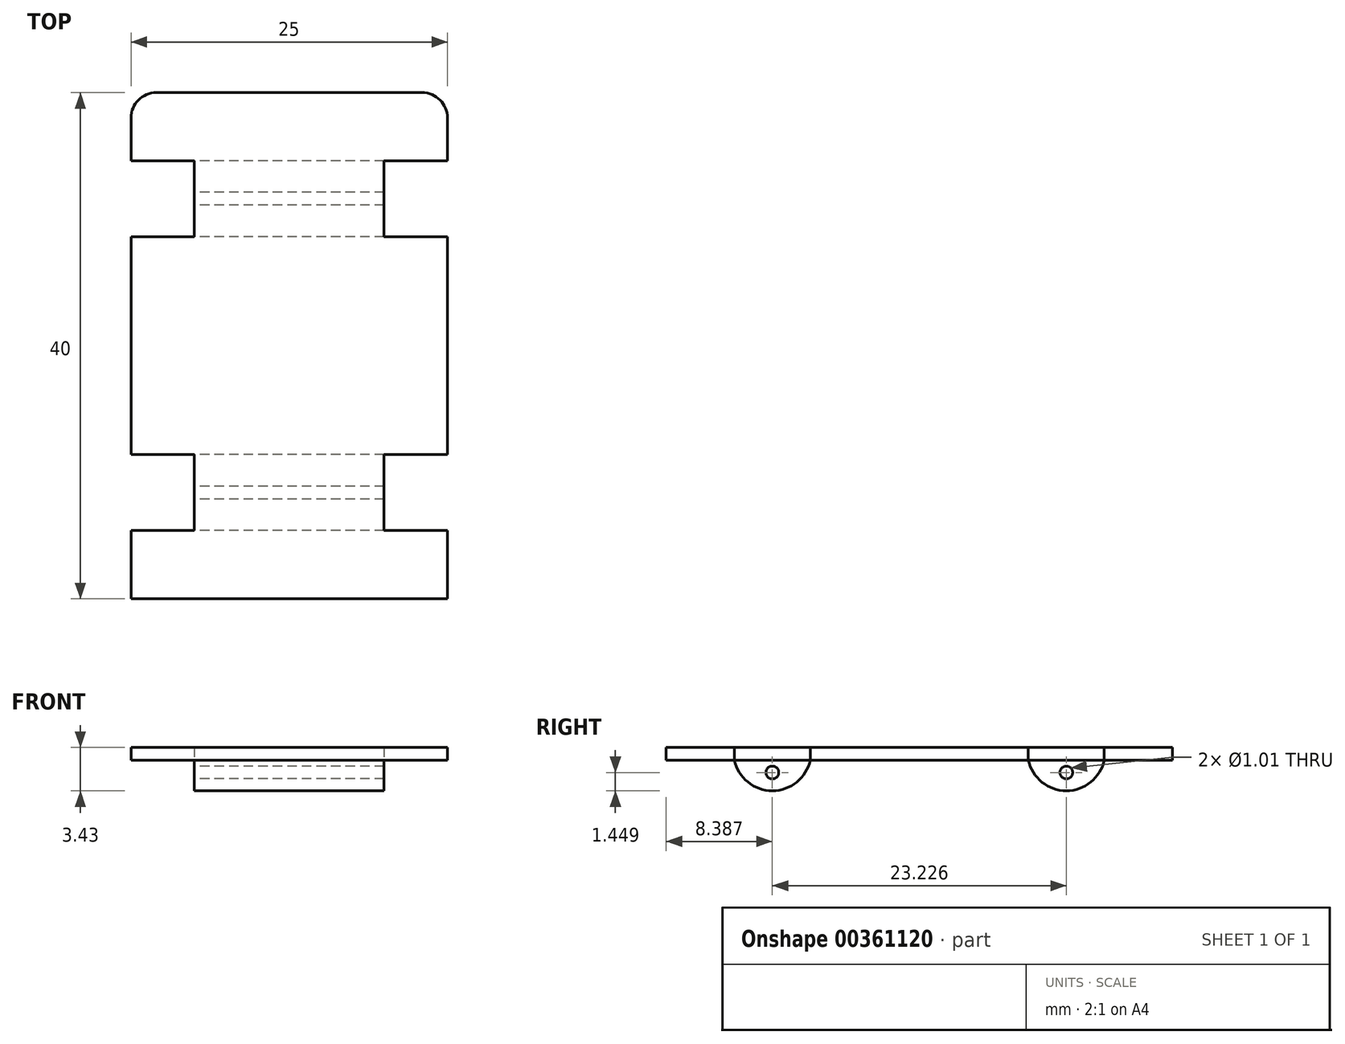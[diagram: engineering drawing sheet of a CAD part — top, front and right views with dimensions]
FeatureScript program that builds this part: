
annotation { "Feature Type Name" : "Feature", "Feature Type Description" : "" }
export const myFeature = defineFeature(function(context is Context, id is Id, definition is map)
    precondition{}
    {
        {
            var Q0;
            Q0=qCreatedBy(makeId("Top.planeOp"),FACE);
            var sketch = newSketch(context, id + "F0", { "sketchPlane" : qUnion([Q0])});
            skLineSegment(sketch, "E0.bottom", {"start": v(10.5, 20) * mm, "end": v(-10.5, 20) * mm});
            skLineSegment(sketch, "E0.top", {"start": v(12.5, -20) * mm, "end": v(-12.5, -20) * mm});
            skLineSegment(sketch, "E0.left", {"start": v(12.5, 18) * mm, "end": v(12.5, 14.61) * mm});
            skLineSegment(sketch, "E0.right", {"start": v(-12.5, 18) * mm, "end": v(-12.5, 14.61) * mm});
            skPoint(sketch, "E0.middle", {"position": v(0, 0) * mm});
            skLineSegment(sketch, "E1.bottom", {"start": v(-12.5, 14.61) * mm, "end": v(-7.5, 14.61) * mm});
            skLineSegment(sketch, "E1.top", {"start": v(-12.5, 8.61) * mm, "end": v(-7.5, 8.61) * mm});
            skLineSegment(sketch, "E1.right", {"start": v(-7.5, 14.61) * mm, "end": v(-7.5, 8.61) * mm});
            skLineSegment(sketch, "E2.MirrorCS", {"start": v(12.5, 14.61) * mm, "end": v(7.5, 14.61) * mm});
            skLineSegment(sketch, "E3.MirrorCS", {"start": v(7.5, 14.61) * mm, "end": v(7.5, 8.61) * mm});
            skLineSegment(sketch, "E4.MirrorCS", {"start": v(12.5, 8.61) * mm, "end": v(7.5, 8.61) * mm});
            skLineSegment(sketch, "E5.MirrorCS", {"start": v(-12.5, -14.61) * mm, "end": v(-7.5, -14.61) * mm});
            skLineSegment(sketch, "E6.MirrorCS", {"start": v(-7.5, -14.61) * mm, "end": v(-7.5, -8.61) * mm});
            skLineSegment(sketch, "E7.MirrorCS", {"start": v(-12.5, -8.61) * mm, "end": v(-7.5, -8.61) * mm});
            skLineSegment(sketch, "E8.MirrorCS", {"start": v(12.5, -14.61) * mm, "end": v(7.5, -14.61) * mm});
            skLineSegment(sketch, "E9.MirrorCS", {"start": v(7.5, -14.61) * mm, "end": v(7.5, -8.61) * mm});
            skLineSegment(sketch, "E10.MirrorCS", {"start": v(12.5, -8.61) * mm, "end": v(7.5, -8.61) * mm});
            skLineSegment(sketch, "E11.trimOffspring", {"start": v(-12.5, 8.61) * mm, "end": v(-12.5, -8.61) * mm});
            skLineSegment(sketch, "E12.trimOffspring", {"start": v(12.5, 8.61) * mm, "end": v(12.5, -8.61) * mm});
            skLineSegment(sketch, "E13.trimOffspring", {"start": v(12.5, -14.61) * mm, "end": v(12.5, -20) * mm});
            skLineSegment(sketch, "E14.trimOffspring", {"start": v(-12.5, -14.61) * mm, "end": v(-12.5, -20) * mm});
            skPoint(sketch, "E15.visualSharp", {"position": v(-12.5, 20) * mm});
            skArc(sketch, "E15.filletArc", {"start": v(-10.5, 20) * mm, "mid": v(-11.91, 19.41) * mm, "end": v(-12.5, 18) * mm});
            skPoint(sketch, "E16.visualSharp", {"position": v(12.5, 20) * mm});
            skArc(sketch, "E16.filletArc", {"start": v(12.5, 18) * mm, "mid": v(11.91, 19.41) * mm, "end": v(10.5, 20) * mm});
            skSolve(sketch);
        }
        {
            var Q0;
            Q0 = qSketchRegion(id + "F0", true);
            extrude(context, id + "F1", {"entities" : qUnion([Q0]), "endBound" : BoundingType.SYMMETRIC, "depth" : 1 * mm});
        }
        {
            var Q0;
            Q0=qCreatedBy(makeId("Right.planeOp"),FACE);
            var sketch = newSketch(context, id + "F2", { "sketchPlane" : qUnion([Q0])});
            skArc(sketch, "E17", {"start": v(-14.62, -0.5) * mm, "mid": v(-11.62, -2.93) * mm, "end": v(-8.61, -0.5) * mm});
            skLineSegment(sketch, "E18", {"start": v(-14.62, -0.5) * mm, "end": v(-8.61, -0.5) * mm});
            skCircle(sketch, "E19", {"center": v(-11.61, -1.48) * mm, "radius": 0.5 * mm});
            skArc(sketch, "E20.MirrorCS", {"start": v(14.62, -0.5) * mm, "mid": v(11.62, -2.93) * mm, "end": v(8.61, -0.5) * mm});
            skCircle(sketch, "E21.MirrorC", {"center": v(11.61, -1.48) * mm, "radius": 0.5 * mm});
            skLineSegment(sketch, "E22.MirrorCS", {"start": v(14.62, -0.5) * mm, "end": v(8.61, -0.5) * mm});
            skSolve(sketch);
        }
        {
            var Q0;
            Q0 = qSketchRegion(id + "F2", true);
            extrude(context, id + "F3", {"entities" : qUnion([Q0]), "endBound" : BoundingType.SYMMETRIC, "depth" : 15 * mm});
        }
    });
